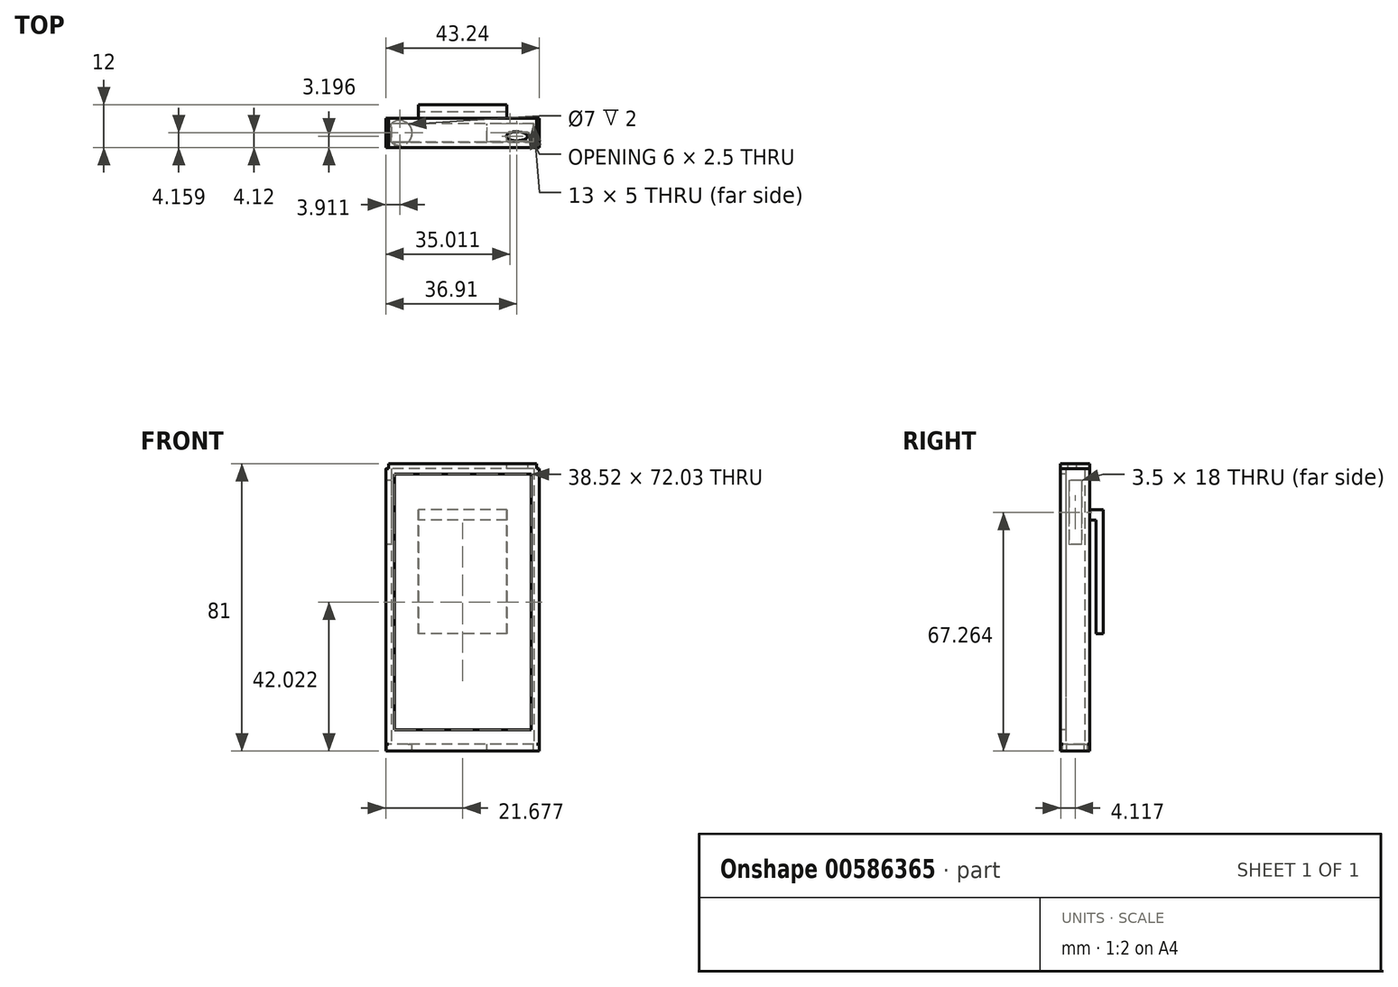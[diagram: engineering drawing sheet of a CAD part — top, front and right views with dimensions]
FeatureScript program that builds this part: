
annotation { "Feature Type Name" : "Feature", "Feature Type Description" : "" }
export const myFeature = defineFeature(function(context is Context, id is Id, definition is map)
    precondition{}
    {
        {
            var Q0;
            Q0=qCreatedBy(makeId("Top.planeOp"),FACE);
            var sketch = newSketch(context, id + "F0", { "sketchPlane" : qUnion([Q0])});
            skLineSegment(sketch, "E0.bottom", {"start": v(20.12, -2.62) * mm, "end": v(-20.12, -2.63) * mm});
            skLineSegment(sketch, "E0.top", {"start": v(20.12, 2.63) * mm, "end": v(-20.12, 2.62) * mm});
            skLineSegment(sketch, "E0.left", {"start": v(20.12, -2.62) * mm, "end": v(20.12, 2.63) * mm});
            skLineSegment(sketch, "E0.right", {"start": v(-20.12, -2.63) * mm, "end": v(-20.12, 2.62) * mm});
            skPoint(sketch, "E0.middle", {"position": v(0, 0) * mm});
            skLineSegment(sketch, "E1.0", {"start": v(-21.63, -3.38) * mm, "end": v(-21.63, 3.37) * mm});
            skLineSegment(sketch, "E1.1", {"start": v(20.88, -4.12) * mm, "end": v(-20.88, -4.13) * mm});
            skLineSegment(sketch, "E1.2", {"start": v(21.63, -3.37) * mm, "end": v(21.63, 3.38) * mm});
            skLineSegment(sketch, "E1.3", {"start": v(20.88, 4.13) * mm, "end": v(-20.88, 4.12) * mm});
            skPoint(sketch, "E2.visualSharp", {"position": v(-21.63, 4.12) * mm});
            skArc(sketch, "E2.filletArc", {"start": v(-20.88, 4.12) * mm, "mid": v(-21.4, 3.9) * mm, "end": v(-21.63, 3.37) * mm});
            skPoint(sketch, "E3.visualSharp", {"position": v(-21.63, -4.13) * mm});
            skArc(sketch, "E3.filletArc", {"start": v(-21.63, -3.38) * mm, "mid": v(-21.4, -3.9) * mm, "end": v(-20.88, -4.13) * mm});
            skPoint(sketch, "E4.visualSharp", {"position": v(21.63, -4.12) * mm});
            skArc(sketch, "E4.filletArc", {"start": v(20.88, -4.12) * mm, "mid": v(21.4, -3.9) * mm, "end": v(21.63, -3.37) * mm});
            skPoint(sketch, "E5.visualSharp", {"position": v(21.63, 4.13) * mm});
            skArc(sketch, "E5.filletArc", {"start": v(21.63, 3.38) * mm, "mid": v(21.4, 3.9) * mm, "end": v(20.88, 4.13) * mm});
            skSolve(sketch);
        }
        {
            var Q0;
            Q0 = qSketchRegion(id + "F0", true);
            extrude(context, id + "F1", {"entities" : qUnion([Q0]), "depth" : 77.5 * mm, "offsetDistance" : 25 * mm});
        }
        {
            var Q0;
            Q0=makeQuery(id+"F1.opExtrude","SWEPT_FACE",FACE,{"disambiguationData":[OSD([sQuery(id+"F0.wireOp",EDGE,"E1.1")])]});
            var sketch = newSketch(context, id + "F2", { "sketchPlane" : qUnion([Q0])});
            skLineSegment(sketch, "E6.bottom", {"start": v(-19.2, 76.04) * mm, "end": v(19.32, 76.04) * mm});
            skLineSegment(sketch, "E6.top", {"start": v(-19.2, 4) * mm, "end": v(19.32, 4) * mm});
            skLineSegment(sketch, "E6.left", {"start": v(-19.2, 76.04) * mm, "end": v(-19.2, 4) * mm});
            skLineSegment(sketch, "E6.right", {"start": v(19.32, 76.04) * mm, "end": v(19.32, 4) * mm});
            skSolve(sketch);
        }
        {
            var Q0;
            Q0=makeQuery(id+"F2.imprint","IMPRINT",FACE,{"disambiguationData":[TD([[makeQuery(id+"F2.imprint","IMPRINT",EDGE,{"derivedFrom":sQuery(id+"F2.wireOp",EDGE,"E6.bottom")}),-1.0]])]});
            extrude(context, id + "F3", {"entities" : qUnion([Q0]), "operationType" : NewBodyOperationType.REMOVE, "oppositeDirection" : true, "depth" : 5 * mm, "offsetDistance" : 25 * mm});
        }
        {
            var Q0;
            Q0=makeQuery(id+"F1.opExtrude","CAP_FACE",FACE,{"disambiguationData":[OSD([sQuery(id+"F0.wireOp",EDGE,"E0.bottom"),sQuery(id+"F0.wireOp",EDGE,"E0.top"),sQuery(id+"F0.wireOp",EDGE,"E0.left"),sQuery(id+"F0.wireOp",EDGE,"E0.right"),sQuery(id+"F0.wireOp",EDGE,"E1.0"),sQuery(id+"F0.wireOp",EDGE,"E1.1"),sQuery(id+"F0.wireOp",EDGE,"E1.2"),sQuery(id+"F0.wireOp",EDGE,"E1.3"),sQuery(id+"F0.wireOp",EDGE,"E2.filletArc"),sQuery(id+"F0.wireOp",EDGE,"E3.filletArc"),sQuery(id+"F0.wireOp",EDGE,"E4.filletArc"),sQuery(id+"F0.wireOp",EDGE,"E5.filletArc")])],"isStart":false});
            var sketch = newSketch(context, id + "F4", { "sketchPlane" : qUnion([Q0])});
            skLineSegment(sketch, "E7.bottom", {"start": v(-20.88, 4.12) * mm, "end": v(20.88, 4.12) * mm});
            skLineSegment(sketch, "E7.top", {"start": v(-20.88, -4.12) * mm, "end": v(20.88, -4.12) * mm});
            skLineSegment(sketch, "E7.left", {"start": v(-20.88, 4.12) * mm, "end": v(-20.88, -4.12) * mm});
            skLineSegment(sketch, "E7.right", {"start": v(20.88, 4.12) * mm, "end": v(20.88, -4.12) * mm});
            skEllipse(sketch, "E8", {"center": v(15.3, -0.92) * mm, "majorRadius": 3 * mm, "minorRadius": 1.25 * mm, "majorAxis": v(1, 0)});
            skSolve(sketch);
        }
        {
            var Q0;
            Q0 = qSketchRegion(id + "F4", true);
            extrude(context, id + "F5", {"entities" : qUnion([Q0]), "operationType" : NewBodyOperationType.ADD, "depth" : 1.5 * mm, "offsetDistance" : 25 * mm});
        }
        {
            var Q0;
            Q0=qCreatedBy(makeId("Top.planeOp"),FACE);
            var sketch = newSketch(context, id + "F6", { "sketchPlane" : qUnion([Q0])});
            skLineSegment(sketch, "E9.bottom", {"start": v(21.63, -4.12) * mm, "end": v(-21.63, -4.13) * mm});
            skLineSegment(sketch, "E9.top", {"start": v(21.63, 4.13) * mm, "end": v(-21.63, 4.12) * mm});
            skLineSegment(sketch, "E9.left", {"start": v(21.63, -4.12) * mm, "end": v(21.63, 4.13) * mm});
            skLineSegment(sketch, "E9.right", {"start": v(-21.63, -4.13) * mm, "end": v(-21.63, 4.12) * mm});
            skCircle(sketch, "E10", {"center": v(-17.7, 0) * mm, "radius": 3.5 * mm});
            skLineSegment(sketch, "E11.bottom", {"start": v(19.9, -2.46) * mm, "end": v(6.9, -2.46) * mm});
            skLineSegment(sketch, "E11.top", {"start": v(19.9, 2.54) * mm, "end": v(6.9, 2.54) * mm});
            skLineSegment(sketch, "E11.left", {"start": v(19.9, -2.46) * mm, "end": v(19.9, 2.54) * mm});
            skLineSegment(sketch, "E11.right", {"start": v(6.9, -2.46) * mm, "end": v(6.9, 2.54) * mm});
            skSolve(sketch);
        }
        {
            var Q0;
            Q0=makeQuery(id+"F6.imprint","IMPRINT",FACE,{"disambiguationData":[TD([[makeQuery(id+"F6.imprint","IMPRINT",EDGE,{"derivedFrom":sQuery(id+"F6.wireOp",EDGE,"E9.bottom")}),-1.0]])]});
            extrude(context, id + "F7", {"entities" : qUnion([Q0]), "operationType" : NewBodyOperationType.ADD, "oppositeDirection" : true, "depth" : 2 * mm, "offsetDistance" : 25 * mm});
        }
        {
            var Q0;
            Q0=makeQuery(id+"F7.boolean.opBoolean","MERGE",FACE,{"derivedFrom":[makeQuery(id+"F1.opExtrude","SWEPT_FACE",FACE,{"disambiguationData":[OSD([sQuery(id+"F0.wireOp",EDGE,"E1.0")])]}),makeQuery(id+"F7.opExtrude","SWEPT_FACE",FACE,{"disambiguationData":[OSD([sQuery(id+"F6.wireOp",EDGE,"E9.right")])]})]});
            var sketch = newSketch(context, id + "F8", { "sketchPlane" : qUnion([Q0])});
            skLineSegment(sketch, "E12.bottom", {"start": v(-1.75, 74.26) * mm, "end": v(1.75, 74.26) * mm});
            skLineSegment(sketch, "E12.top", {"start": v(-1.75, 56.26) * mm, "end": v(1.75, 56.26) * mm});
            skLineSegment(sketch, "E12.left", {"start": v(-1.75, 74.26) * mm, "end": v(-1.75, 56.26) * mm});
            skLineSegment(sketch, "E12.right", {"start": v(1.75, 74.26) * mm, "end": v(1.75, 56.26) * mm});
            skSolve(sketch);
        }
        {
            var Q0;
            Q0=makeQuery(id+"F8.imprint","IMPRINT",FACE,{"disambiguationData":[TD([[makeQuery(id+"F8.imprint","IMPRINT",EDGE,{"derivedFrom":sQuery(id+"F8.wireOp",EDGE,"E12.bottom")}),-1.0]])]});
            extrude(context, id + "F9", {"entities" : qUnion([Q0]), "operationType" : NewBodyOperationType.REMOVE, "oppositeDirection" : true, "depth" : 5 * mm, "offsetDistance" : 25 * mm});
        }
        {
            var Q0;
            Q0=qCreatedBy(makeId("Right.planeOp"),FACE);
            var sketch = newSketch(context, id + "F10", { "sketchPlane" : qUnion([Q0])});
            skLineSegment(sketch, "E13", {"start": v(4.13, 66.05) * mm, "end": v(7.87, 66.05) * mm});
            skLineSegment(sketch, "E14", {"start": v(7.88, 66.05) * mm, "end": v(7.88, 31.05) * mm});
            skLineSegment(sketch, "E15", {"start": v(7.88, 31.05) * mm, "end": v(5.88, 31.05) * mm});
            skLineSegment(sketch, "E16", {"start": v(5.88, 31.05) * mm, "end": v(5.88, 63.05) * mm});
            skLineSegment(sketch, "E17", {"start": v(5.88, 63.05) * mm, "end": v(4.13, 63.05) * mm});
            skLineSegment(sketch, "E18", {"start": v(4.13, 63.05) * mm, "end": v(4.13, 66.05) * mm});
            skSolve(sketch);
        }
        {
            var Q0;
            Q0 = qSketchRegion(id + "F10", true);
            extrude(context, id + "F11", {"entities" : qUnion([Q0]), "operationType" : NewBodyOperationType.ADD, "endBound" : BoundingType.SYMMETRIC, "depth" : 25 * mm, "offsetDistance" : 25 * mm});
        }
    });
